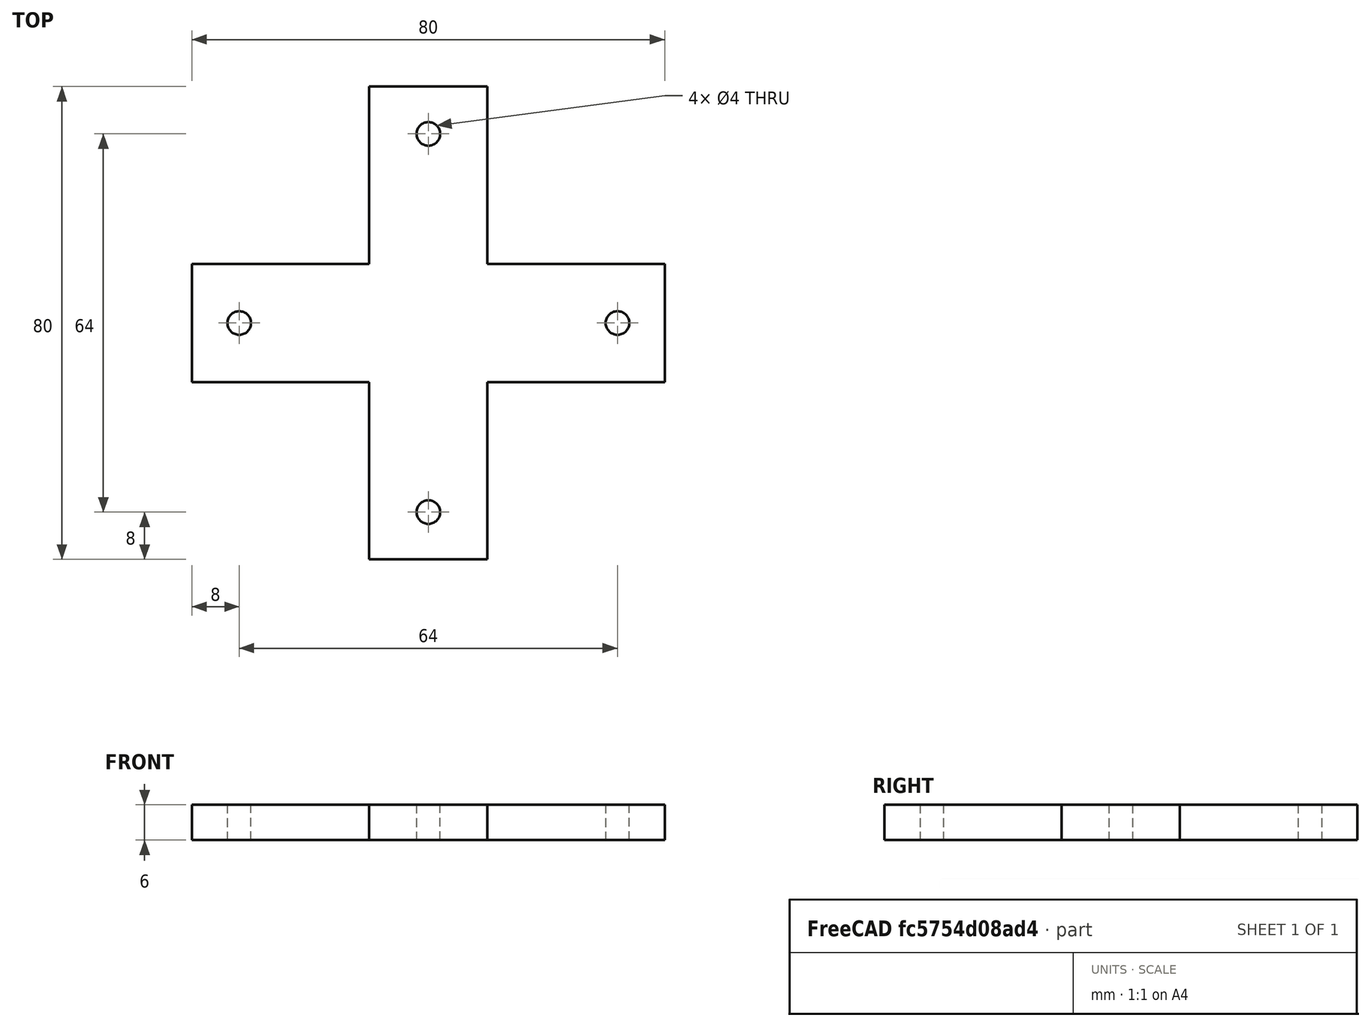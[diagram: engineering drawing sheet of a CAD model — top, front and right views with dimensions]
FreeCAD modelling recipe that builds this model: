
FCSTD DOCUMENT  (FreeCAD 0.21R33771 (Git))
Label: OJT1_T19R02_creu
License: All rights reserved
LicenseURL: http://en.wikipedia.org/wiki/All_rights_reserved
objects: Sketcher::SketchObject×1, PartDesign::Pad×1, PartDesign::Body×1
note: 4 computed .brp shape members not serialized (recipe doc carries the construction recipe); baked Part::Feature solids carry a one-line shape summary decoded from their .brp

FEATURE [Sketcher::SketchObject] Sketch
  FullyConstrained = true
  MapMode = 5
  Support = -> [XY_Plane]
  sketch-geometry (16):
    g0: LineSegment StartX=-10 StartY=40 StartZ=0 EndX=10 EndY=40 EndZ=0
    g1: LineSegment StartX=10 StartY=40 StartZ=0 EndX=10 EndY=10 EndZ=0
    g2: LineSegment StartX=10 StartY=10 StartZ=0 EndX=40 EndY=10 EndZ=0
    g3: LineSegment StartX=40 StartY=10 StartZ=0 EndX=40 EndY=-10 EndZ=0
    g4: LineSegment StartX=40 StartY=-10 StartZ=0 EndX=10 EndY=-10 EndZ=0
    g5: LineSegment StartX=10 StartY=-10 StartZ=0 EndX=10 EndY=-40 EndZ=0
    g6: LineSegment StartX=10 StartY=-40 StartZ=0 EndX=-10 EndY=-40 EndZ=0
    g7: LineSegment StartX=-10 StartY=-40 StartZ=0 EndX=-10 EndY=-10 EndZ=0
    g8: LineSegment StartX=-10 StartY=-10 StartZ=0 EndX=-40 EndY=-10 EndZ=0
    g9: LineSegment StartX=-40 StartY=-10 StartZ=0 EndX=-40 EndY=10 EndZ=0
    g10: LineSegment StartX=-40 StartY=10 StartZ=0 EndX=-10 EndY=10 EndZ=0
    g11: LineSegment StartX=-10 StartY=10 StartZ=0 EndX=-10 EndY=40 EndZ=0
    g12: Circle CenterX=-32 CenterY=0 CenterZ=0 NormalX=0 NormalY=0 NormalZ=1 AngleXU=0 Radius=2
    g13: Circle CenterX=0 CenterY=32 CenterZ=0 NormalX=0 NormalY=0 NormalZ=1 AngleXU=0 Radius=2
    g14: Circle CenterX=32 CenterY=0 CenterZ=0 NormalX=0 NormalY=0 NormalZ=1 AngleXU=0 Radius=2
    g15: Circle CenterX=0 CenterY=-32 CenterZ=0 NormalX=0 NormalY=0 NormalZ=1 AngleXU=0 Radius=2
  constraints (43):
    c: Coincident(g0,g1)
    c: Vertical(g1)
    c: Coincident(g1,g2)
    c: Horizontal(g2)
    c: Coincident(g2,g3)
    c: Coincident(g3,g4)
    c: Horizontal(g4)
    c: Coincident(g4,g5)
    c: Vertical(g5)
    c: Coincident(g5,g6)
    c: Coincident(g6,g7)
    c: Vertical(g7)
    c: Coincident(g7,g8)
    c: Horizontal(g8)
    c: Coincident(g8,g9)
    c: Vertical(g9)
    c: Coincident(g9,g10)
    c: Horizontal(g10)
    c: Coincident(g10,g11)
    c: Coincident(g11,g0)
    c: Vertical(g11)
    c: DistanceY(g8,g9) = 20
    c: Symmetric(g5,g6,g-2)
    c: Symmetric(g2,g9,g-2)
    c: Symmetric(g0,g5,g-1)
    c: Horizontal(g0)
    c: Vertical(g3)
    c: Equal(g10,g11)
    c: Equal(g9,g3)
    c: Equal(g0,g6)
    c: Equal(g9,g6)
    c: Equal(g4,g5)
    c: DistanceX(g8,g3) = 80
    c: PointOnObject(g12,g-1)
    c: Radius(g12) = 2
    c: DistanceX(g9,g12) = 8
    c: PointOnObject(g13,g-2)
    c: Equal(g12,g13)
    c: Equal(g13,g14)
    c: Equal(g14,g15)
    c: Symmetric(g12,g14,g-2)
    c: DistanceY(g13,g0) = 8
    c: Symmetric(g13,g15,g-1)
FEATURE [PartDesign::Pad] Pad
  Direction = (0,0,1)
  Length = 6
  Length2 = 10
  Profile = -> Sketch
  ReferenceAxis = -> Sketch [N_Axis]
  Type = 0
FEATURE [PartDesign::Body] Body
  Group = -> [Sketch,Pad]
  Origin = -> Origin
  Tip = -> Pad
